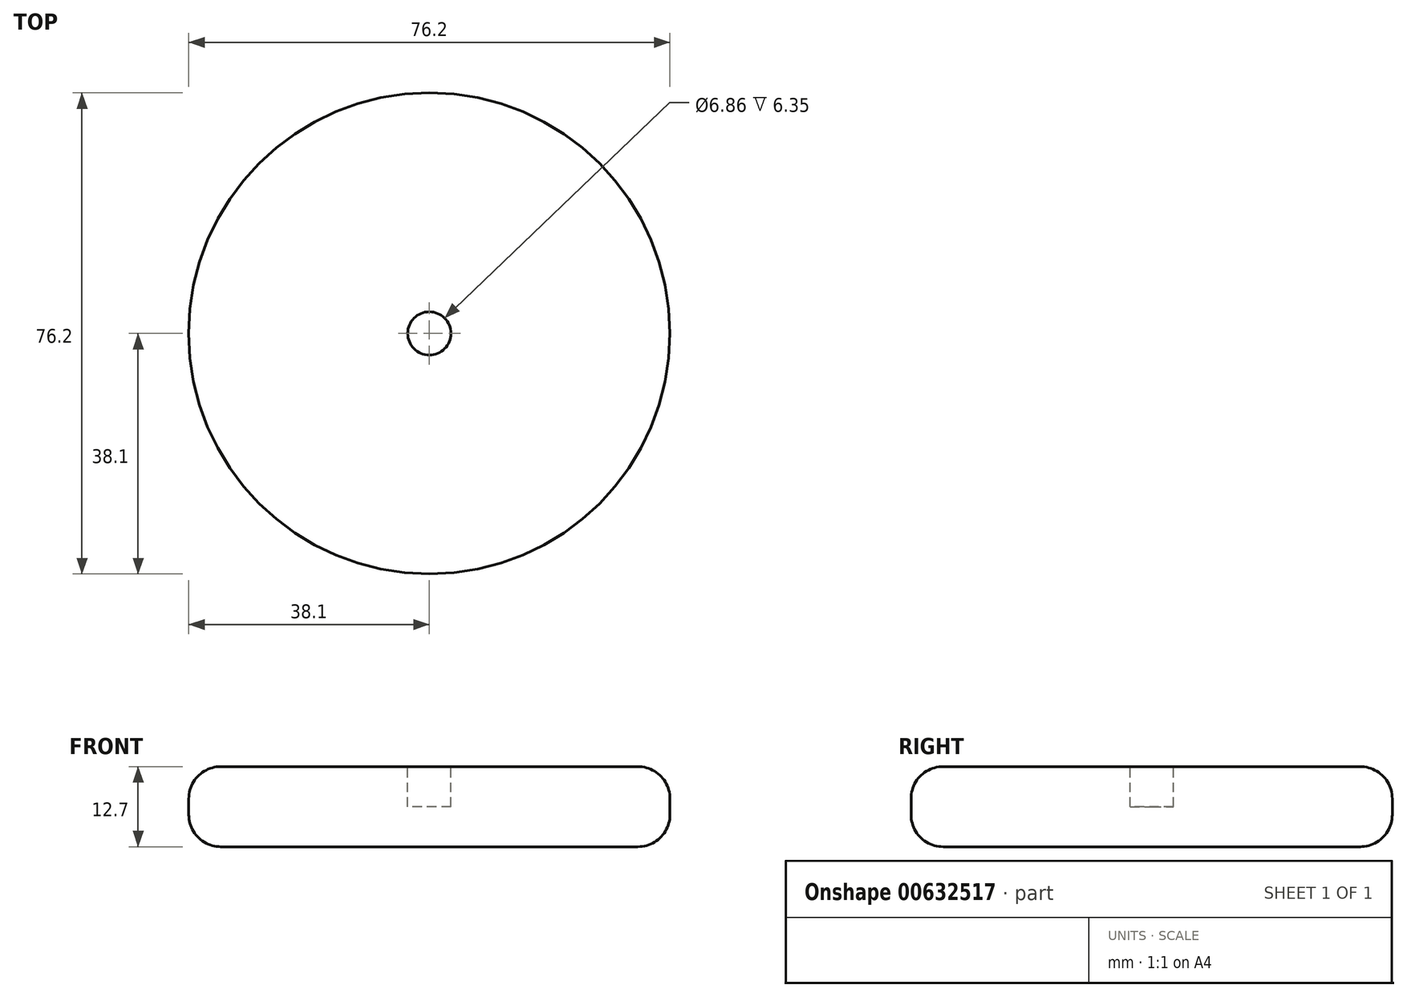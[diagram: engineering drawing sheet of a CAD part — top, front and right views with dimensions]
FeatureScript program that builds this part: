
annotation { "Feature Type Name" : "Feature", "Feature Type Description" : "" }
export const myFeature = defineFeature(function(context is Context, id is Id, definition is map)
    precondition{}
    {
        {
            var Q0;
            Q0=qCreatedBy(makeId("Top.planeOp"),FACE);
            var sketch = newSketch(context, id + "F0", { "sketchPlane" : qUnion([Q0])});
            skCircle(sketch, "E0", {"center": v(0, 0) * mm, "radius": 38.1 * mm});
            skSolve(sketch);
        }
        {
            var Q0;
            Q0=makeQuery(id+"F0.imprint","IMPRINT",FACE,{"disambiguationData":[TD([[makeQuery(id+"F0.imprint","IMPRINT",EDGE,{"derivedFrom":sQuery(id+"F0.wireOp",EDGE,"E0")}),1.0]])]});
            extrude(context, id + "F1", {"entities" : qUnion([Q0]), "depth" : 12.7 * mm, "offsetDistance" : 25.4 * mm});
        }
        {
            var Q0;
            Q0=makeQuery(id+"F1.opExtrude","CAP_EDGE",EDGE,{"disambiguationData":[OSD([sQuery(id+"F0.wireOp",EDGE,"E0")])],"isStart":true});
            var Q1;
            Q1=makeQuery(id+"F1.opExtrude","CAP_EDGE",EDGE,{"disambiguationData":[OSD([sQuery(id+"F0.wireOp",EDGE,"E0")])],"isStart":false});
            fillet(context, id + "F2", {"entities" : qUnion([Q0, Q1]), "radius" : 5.08 * mm, "tangentPropagation" : true, "allowEdgeOverflow" : false});
        }
        {
            var Q0;
            Q0=makeQuery(id+"F1.opExtrude","CAP_FACE",FACE,{"disambiguationData":[OSD([sQuery(id+"F0.wireOp",EDGE,"E0")])],"isStart":false});
            var sketch = newSketch(context, id + "F3", { "sketchPlane" : qUnion([Q0])});
            skCircle(sketch, "E1", {"center": v(0, 0) * mm, "radius": 3.43 * mm});
            skSolve(sketch);
        }
        {
            var Q0;
            Q0 = qSketchRegion(id + "F3", true);
            extrude(context, id + "F4", {"entities" : qUnion([Q0]), "operationType" : NewBodyOperationType.REMOVE, "oppositeDirection" : true, "depth" : 6.35 * mm, "offsetDistance" : 25.4 * mm});
        }
    });
